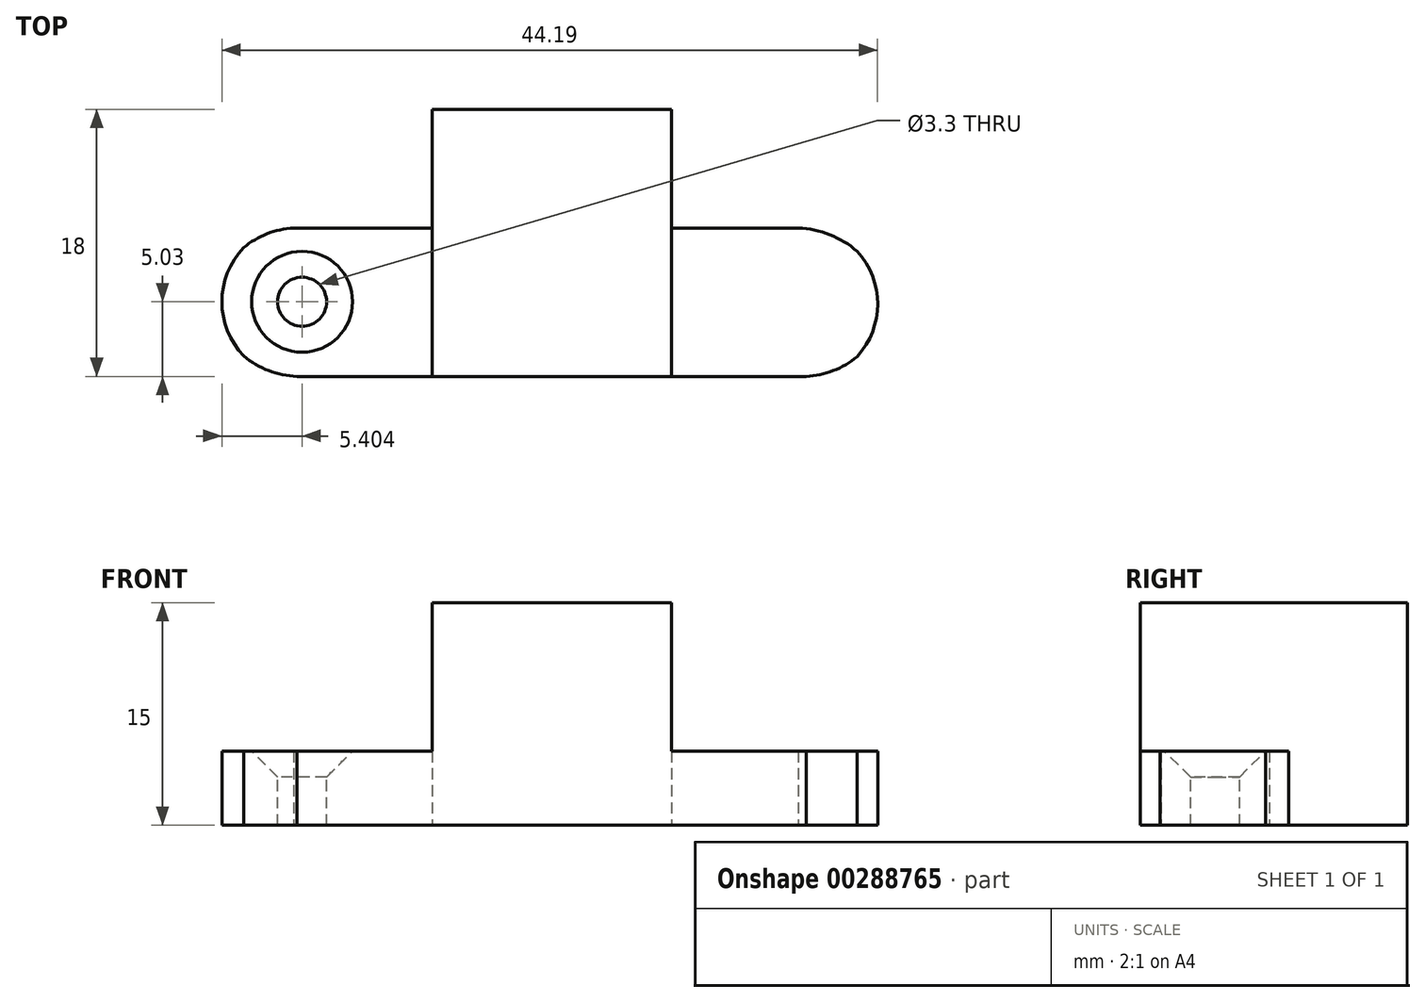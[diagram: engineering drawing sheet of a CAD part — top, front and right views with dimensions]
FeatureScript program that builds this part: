
annotation { "Feature Type Name" : "Feature", "Feature Type Description" : "" }
export const myFeature = defineFeature(function(context is Context, id is Id, definition is map)
    precondition{}
    {
        {
            var Q0;
            Q0=qCreatedBy(makeId("Top.planeOp"),FACE);
            var sketch = newSketch(context, id + "F0", { "sketchPlane" : qUnion([Q0])});
            skLineSegment(sketch, "E0.bottom", {"start": v(-5.47, 0) * mm, "end": v(-39.77, 0) * mm});
            skLineSegment(sketch, "E0.top", {"start": v(-6, 10) * mm, "end": v(-14.53, 10) * mm});
            skCircle(sketch, "E1", {"center": v(-39.4, 5) * mm, "radius": 1.7 * mm});
            skPoint(sketch, "E1.centerSnap0", {"position": v(-45.4, 5) * mm});
            skCircle(sketch, "E2", {"center": v(-6, 5) * mm, "radius": 1.7 * mm});
            skPoint(sketch, "E2.centerSnap0", {"position": v(0, 5) * mm});
            skArc(sketch, "E3", {"start": v(-39.39, 10) * mm, "mid": v(-41.5, 9.72) * mm, "end": v(-43.37, 8.68) * mm});
            skArc(sketch, "E4", {"start": v(-43.37, 1.38) * mm, "mid": v(-41.51, 0.32) * mm, "end": v(-39.4, 0) * mm});
            skArc(sketch, "E5", {"start": v(-43.37, 8.68) * mm, "mid": v(-44.84, 5.03) * mm, "end": v(-43.37, 1.38) * mm});
            skPoint(sketch, "E5.endSnap0", {"position": v(-43.37, 8.68) * mm});
            skPoint(sketch, "E6.orphan", {"position": v(-45.4, 10) * mm});
            skPoint(sketch, "E7.orphan", {"position": v(-45.4, 0) * mm});
            skArc(sketch, "E8", {"start": v(-2.03, 8.43) * mm, "mid": v(-3.88, 9.56) * mm, "end": v(-6, 10) * mm});
            skArc(sketch, "E9", {"start": v(-6, 0) * mm, "mid": v(-3.89, 0.3) * mm, "end": v(-2.03, 1.34) * mm});
            skArc(sketch, "E10", {"start": v(-2.03, 1.34) * mm, "mid": v(-0.65, 4.88) * mm, "end": v(-2.03, 8.43) * mm});
            skPoint(sketch, "E10.endSnap0", {"position": v(-2.03, 1.34) * mm});
            skPoint(sketch, "E11.orphan", {"position": v(0, 10) * mm});
            skPoint(sketch, "E12.orphan", {"position": v(0, 0) * mm});
            skLineSegment(sketch, "E13.top", {"start": v(-30.65, 18) * mm, "end": v(-14.53, 18) * mm});
            skLineSegment(sketch, "E13.left", {"start": v(-30.65, 10) * mm, "end": v(-30.65, 18) * mm});
            skLineSegment(sketch, "E13.right", {"start": v(-14.53, 10) * mm, "end": v(-14.53, 18) * mm});
            skLineSegment(sketch, "E14", {"start": v(-30.65, 10) * mm, "end": v(-30.65, 0) * mm});
            skLineSegment(sketch, "E15", {"start": v(-30.65, 0) * mm, "end": v(-14.53, 0) * mm});
            skLineSegment(sketch, "E16", {"start": v(-14.53, 0) * mm, "end": v(-14.53, 10) * mm});
            skLineSegment(sketch, "E17.trimOffspring", {"start": v(-30.65, 10) * mm, "end": v(-40, 10) * mm});
            skSolve(sketch);
        }
        {
            var Q0;
            Q0=makeQuery(id+"F0.imprint","IMPRINT",FACE,{"disambiguationData":[TD([[makeQuery(id+"F0.imprint","IMPRINT",EDGE,{"derivedFrom":sQuery(id+"F0.wireOp",EDGE,"E1")}),-1.0]])]});
            var Q1;
            Q1=makeQuery(id+"F0.imprint","IMPRINT",FACE,{"disambiguationData":[TD([[makeQuery(id+"F0.imprint","IMPRINT",EDGE,{"derivedFrom":sQuery(id+"F0.wireOp",EDGE,"E13.top")}),-1.0]])]});
            var Q2;
            Q2=makeQuery(id+"F0.imprint","IMPRINT",FACE,{"disambiguationData":[TD([[makeQuery(id+"F0.imprint","IMPRINT",EDGE,{"derivedFrom":sQuery(id+"F0.wireOp",EDGE,"E0.top")}),1.0]])]});
            var Q3;
            Q3=makeQuery(id+"F0.imprint","IMPRINT",FACE,{"disambiguationData":[TD([[makeQuery(id+"F0.imprint","IMPRINT",EDGE,{"derivedFrom":sQuery(id+"F0.wireOp",EDGE,"E1")}),1.0]])]});
            var Q4;
            Q4=makeQuery(id+"F0.imprint","IMPRINT",FACE,{"disambiguationData":[TD([[makeQuery(id+"F0.imprint","IMPRINT",EDGE,{"derivedFrom":sQuery(id+"F0.wireOp",EDGE,"E2")}),1.0]])]});
            extrude(context, id + "F1", {"entities" : qUnion([Q0, Q1, Q2, Q3, Q4]), "depth" : 5 * mm});
        }
        {
            var Q0;
            Q0=makeQuery(id+"F0.imprint","IMPRINT",FACE,{"disambiguationData":[TD([[makeQuery(id+"F0.imprint","IMPRINT",EDGE,{"derivedFrom":sQuery(id+"F0.wireOp",EDGE,"E13.top")}),-1.0]])]});
            extrude(context, id + "F2", {"entities" : qUnion([Q0]), "operationType" : NewBodyOperationType.ADD, "depth" : 15 * mm});
        }
        {
            var Q0;
            {var subQ0=sQuery(id+"F0.wireOp",EDGE,"E5");var subQ1=sQuery(id+"F0.wireOp",EDGE,"E4");var subQ2=sQuery(id+"F0.wireOp",EDGE,"E3");var subQ3=sQuery(id+"F0.wireOp",EDGE,"E15");var subQ4=sQuery(id+"F0.wireOp",EDGE,"E0.bottom");var subQ5=sQuery(id+"F0.wireOp",EDGE,"E17.trimOffspring");var subQ6=sQuery(id+"F0.wireOp",EDGE,"E13.left");Q0=makeQuery(id+"F2.boolean.opBoolean","SPLIT",FACE,{"disambiguationData":[TD([makeQuery(id+"F1.opExtrude","SWEPT_FACE",FACE,{"disambiguationData":[OSD([subQ2])]})])],"derivedFrom":makeQuery(id+"F1.opExtrude","CAP_FACE",FACE,{"disambiguationData":[OSD([subQ4,sQuery(id+"F0.wireOp",EDGE,"E0.top"),subQ2,subQ1,subQ0,sQuery(id+"F0.wireOp",EDGE,"E8"),sQuery(id+"F0.wireOp",EDGE,"E9"),sQuery(id+"F0.wireOp",EDGE,"E10"),sQuery(id+"F0.wireOp",EDGE,"E13.top"),subQ6,sQuery(id+"F0.wireOp",EDGE,"E13.right"),subQ3,subQ5])],"isStart":false})});}
            var sketch = newSketch(context, id + "F3", { "sketchPlane" : qUnion([Q0])});
            skCircle(sketch, "E18", {"center": v(-39.44, 5.03) * mm, "radius": 1.5 * mm});
            skPoint(sketch, "E18.centerSnap0", {"position": v(-44.84, 5.03) * mm});
            skCircle(sketch, "E19", {"center": v(-6.04, 5.03) * mm, "radius": 1.54 * mm});
            skSolve(sketch);
        }
        {
            var Q0;
            Q0=sQuery(id+"F3.wireOp",VERTEX,"E18.center");
            var Q1;
            Q1=makeQuery(id+"F1.opExtrude","SWEPT_BODY",BODY,{"disambiguationData":[OSD([sQuery(id+"F0.wireOp",EDGE,"E0.bottom"),sQuery(id+"F0.wireOp",EDGE,"E0.top"),sQuery(id+"F0.wireOp",EDGE,"E3"),sQuery(id+"F0.wireOp",EDGE,"E4"),sQuery(id+"F0.wireOp",EDGE,"E5"),sQuery(id+"F0.wireOp",EDGE,"E8"),sQuery(id+"F0.wireOp",EDGE,"E9"),sQuery(id+"F0.wireOp",EDGE,"E10"),sQuery(id+"F0.wireOp",EDGE,"E13.top"),sQuery(id+"F0.wireOp",EDGE,"E13.left"),sQuery(id+"F0.wireOp",EDGE,"E13.right"),sQuery(id+"F0.wireOp",EDGE,"E15"),sQuery(id+"F0.wireOp",EDGE,"E17.trimOffspring")])]});
            hole(context, id + "F4", {"style" : HoleStyle.C_SINK, "endStyle" : HoleEndStyle.THROUGH, "holeDiameter" : 3.3 * mm, "cSinkDiameter" : 6.8 * mm, "cSinkAngle" : 90 * degree, "tappedDepth" : 12 * mm, "tapClearance" : 3, "locations" : qUnion([Q0]), "scope" : qUnion([Q1])});
        }
    });
